# Revit family: Stex 35 Gewindebolzen GB
name_source: partatom
category: HLS-Bauteile
revit_build: Autodesk Revit 2017 (Build: 20190507_1515(x64)
units: mm (PartAtom-declared; Revit-internal decimal feet)

## family parameters
Arbeitsebenenbasiert = Ja
Beim Laden mit Abzugskörper schneiden = Nein
Bemaßung runder Anschluss = Durchmesser verwenden
Gemeinsam genutzt = Ja
Immer vertikal = Nein
Raumberechnungspunkt = Nein
Teiletyp = Normal

## types (10) — shared parameters
Anzugsmoment = 0.00 kN-m
Fabrikat = MEFA
Firma = MEFA Befestigungs- und Montagesysteme GmbH
Kurztext1 = Stex Gewindebolzen 35
Material = Stahl
Materialname = S235
Mengeneinheit = St
Oberflaeche = galvanisch verzinkt
Vorgabe-Ansicht = 1219 mm
max. zul. Last = 0.00 kN

## per-type parameters (varying)
| type | Abmessung | Artikelnummer | EAN | Gewicht | Gewicht pro Bauteil | Gewinde | Gewindeplatte | Gewindestift | Kurztext2 | Länge Gewinde | Nutzlänge | Sechskantmutter | vpe |
| Stex-Gewindebolzen M10x 50 | M10 x 50 mm | 127005001 | 4250928424266 | 0.08 kg | 0.08 kg | M10 | MEFA Gewindeplatte 35 für Stex 35 : MEFA Gewindeplatte 35 für Stex 35 M10 | MEFA Gewindestifte : Gewindestift M10x 50 | M10 x 50 mm | 50 mm  [stored 0.164042 ft] | 34 mm | MEFA Sechskantmutter : Sechskantmutter M10 | 50 St |
| Stex-Gewindebolzen M 8x 50 | M8 x 50 mm | 127805001 | 4250928424600 | 0.06 kg | 0.06 kg | M8 | MEFA Gewindeplatte 35 für Stex 35 : MEFA Gewindeplatte 35 für Stex 35 M 8 | MEFA Gewindestifte : Gewindestift M 8x 50 | M8 x 50 mm | 50 mm  [stored 0.164042 ft] | 36 mm | MEFA Sechskantmutter : Sechskantmutter M 8 | 50 St |
| Stex-Gewindebolzen M10x 70 | M10 x 70 mm | 127007001 | 4250928424273 | 0.09 kg | 0.09 kg | M10 | MEFA Gewindeplatte 35 für Stex 35 : MEFA Gewindeplatte 35 für Stex 35 M10 | MEFA Gewindestifte : Gewindestift M10x 70 | M10 x 70 mm | 70 mm  [stored 0.229659 ft] | 54 mm | MEFA Sechskantmutter : Sechskantmutter M10 | 50 St |
| Stex-Gewindebolzen M10x 90 | M10 x 90 mm | 127009001 | 4250928424280 | 0.10 kg | 0.10 kg | M10 | MEFA Gewindeplatte 35 für Stex 35 : MEFA Gewindeplatte 35 für Stex 35 M10 | MEFA Gewindestifte : Gewindestift M10x 90 | M10 x 90 mm | 90 mm  [stored 0.295276 ft] | 74 mm | MEFA Sechskantmutter : Sechskantmutter M10 | 50 St |
| Stex-Gewindebolzen M10x110 | M10 x 110 mm | 127011001 | 4250928424297 | 0.11 kg | 0.11 kg | M10 | MEFA Gewindeplatte 35 für Stex 35 : MEFA Gewindeplatte 35 für Stex 35 M10 | MEFA Gewindestifte : Gewindestift M10x110 | M10 x 110 mm | 110 mm  [stored 0.360892 ft] | 94 mm | MEFA Sechskantmutter : Sechskantmutter M10 | 25 St |
| Stex-Gewindebolzen M10x130 | M10 x 130 mm | 127013001 | 4250928424303 | 0.12 kg | 0.12 kg | M10 | MEFA Gewindeplatte 35 für Stex 35 : MEFA Gewindeplatte 35 für Stex 35 M10 | MEFA Gewindestifte : Gewindestift M10x130 | M10 x 130 mm | 130 mm  [stored 0.426509 ft] | 114 mm | MEFA Sechskantmutter : Sechskantmutter M10 | 25 St |
| Stex-Gewindebolzen M 8x 70 | M8 x 70 mm | 127807001 | 4250928424617 | 0.07 kg | 0.07 kg | M8 | MEFA Gewindeplatte 35 für Stex 35 : MEFA Gewindeplatte 35 für Stex 35 M 8 | MEFA Gewindestifte : Gewindestift M 8x 70 | M8 x 70 mm | 70 mm  [stored 0.229659 ft] | 56 mm | MEFA Sechskantmutter : Sechskantmutter M 8 | 50 St |
| Stex-Gewindebolzen M 8x 90 | M8 x 90 mm | 127809001 | 4250928424624 | 0.07 kg | 0.07 kg | M8 | MEFA Gewindeplatte 35 für Stex 35 : MEFA Gewindeplatte 35 für Stex 35 M 8 | MEFA Gewindestifte : Gewindestift M 8x 90 | M8 x 90 mm | 90 mm  [stored 0.295276 ft] | 76 mm | MEFA Sechskantmutter : Sechskantmutter M 8 | 50 St |
| Stex-Gewindebolzen M 8x110 | M8 x 110 mm | 127811001 | 4250928424631 | 0.08 kg | 0.08 kg | M8 | MEFA Gewindeplatte 35 für Stex 35 : MEFA Gewindeplatte 35 für Stex 35 M 8 | MEFA Gewindestifte : Gewindestift M 8x110 | M8 x 110 mm | 110 mm  [stored 0.360892 ft] | 96 mm | MEFA Sechskantmutter : Sechskantmutter M 8 | 25 St |
| Stex-Gewindebolzen M 8x130 | M8 x 130 mm | 127813001 | 4250928424648 | 0.09 kg | 0.09 kg | M8 | MEFA Gewindeplatte 35 für Stex 35 : MEFA Gewindeplatte 35 für Stex 35 M 8 | MEFA Gewindestifte : Gewindestift M 8x130 | M8 x 130 mm | 130 mm  [stored 0.426509 ft] | 116 mm | MEFA Sechskantmutter : Sechskantmutter M 8 | 25 St |

note: [stored X ft] marks values corroborated as IEEE doubles in the binary element streams (Revit-internal decimal feet)

## geometry (parser evidence)
native form markers: Sweep x3
no freeform markers — native parametric forms only
